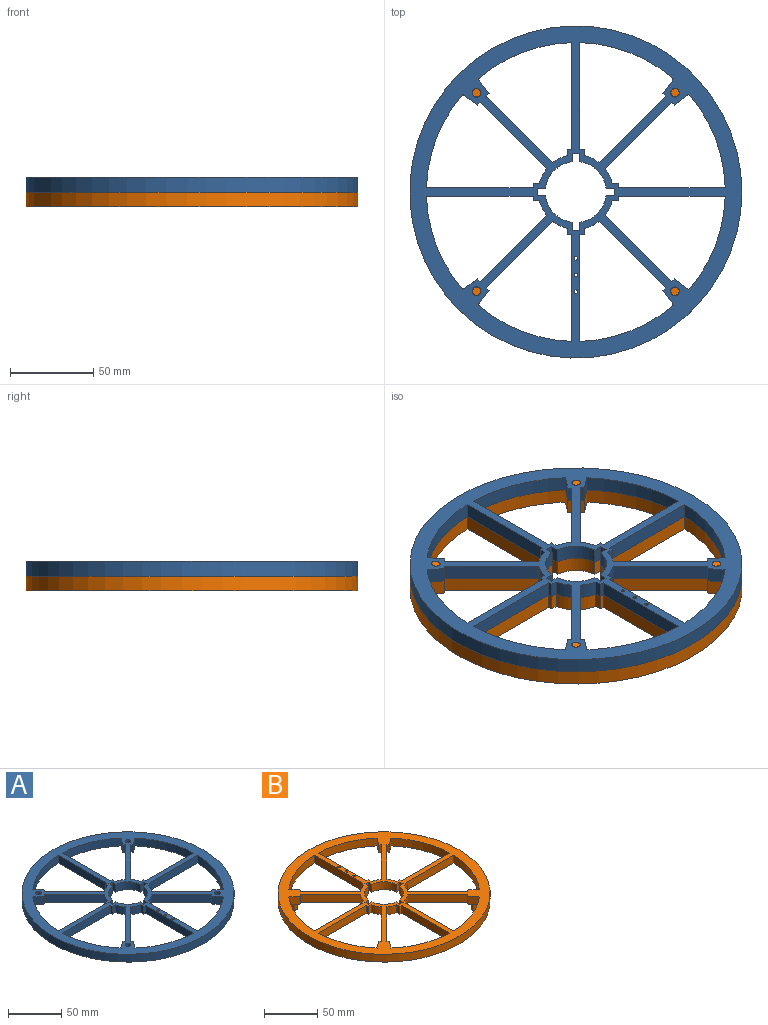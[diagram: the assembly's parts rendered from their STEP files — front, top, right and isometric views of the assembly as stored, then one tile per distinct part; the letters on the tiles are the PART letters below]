
ASSEMBLY  parts=2 mates=1
PART A: 94 faces, bbox 200x200x9 mm
  f0: plane 188.8x188.8mm, normal (0,0,-1), area 5946.6mm2, adj f1,f2,f3,f4,f5,f6,f7,f8
  f1: plane 40.07x40.07mm, normal (-0.71,0.71,0), area 510mm2, adj f0,f2,f75,f89
  f2: plane 9x1.78mm, normal (0.7,0.71,0), area 22.5mm2, adj f0,f1,f3,f89
  f3: plane 9x8.64mm, normal (-0.6,0.8,0), area 97.4mm2, adj f0,f2,f4,f89
  f4: cylinder r=90mm len=56.38mm, axis (0,0,-1), area 555.1mm2, adj f0,f3,f5,f89
  f5: plane 64.26x9mm, normal (0,-1,0), area 578.3mm2, adj f0,f4,f6,f89
  f6: plane 9x2.5mm, normal (-1,0,0), area 22.5mm2, adj f0,f5,f7,f89
  f7: plane 9x3.77mm, normal (0,-1,0), area 33.9mm2, adj f0,f6,f75,f89
  f8: plane 40.07x40.07mm, normal (0.71,0.71,0), area 510mm2, adj f0,f9,f76,f89
  f9: plane 9x1.78mm, normal (0.71,-0.7,0), area 22.5mm2, adj f0,f8,f10,f89
  f10: plane 9x8.64mm, normal (0.8,0.6,0), area 97.4mm2, adj f0,f9,f11,f89
  f11: cylinder r=90mm len=56.38mm, axis (0,0,-1), area 555.1mm2, adj f0,f10,f12,f89
  f12: plane 64.26x9mm, normal (-1,0,0), area 578.3mm2, adj f0,f11,f13,f89
  f13: plane 9x2.5mm, normal (0,1,0), area 22.5mm2, adj f0,f12,f14,f89
  f14: plane 9x3.77mm, normal (-1,0,0), area 33.9mm2, adj f0,f13,f76,f89
  f15: plane 9x5.02mm, normal (0,1,0), area 45.2mm2, adj f0,f16,f79,f89
  f16: cylinder r=18.4mm len=16.07mm, axis (0,0,-1), area 220.4mm2, adj f0,f15,f17,f89
  f17: plane 9x5.02mm, normal (-1,0,0), area 45.2mm2, adj f0,f16,f18,f89
  f18: plane 9x4.4mm, normal (0,1,0), area 39.6mm2, adj f0,f17,f19,f89
  f19: plane 9x5.02mm, normal (1,0,0), area 45.2mm2, adj f0,f18,f20,f89
  f20: cylinder r=18.4mm len=16.07mm, axis (0,0,-1), area 220.4mm2, adj f0,f19,f21,f89
  f21: plane 9x5.02mm, normal (0,1,0), area 45.2mm2, adj f0,f20,f22,f89
  f22: plane 9x4.4mm, normal (1,0,0), area 39.6mm2, adj f0,f21,f23,f89
  f23: plane 9x5.02mm, normal (0,-1,0), area 45.2mm2, adj f0,f22,f24,f89
  f24: cylinder r=18.4mm len=16.07mm, axis (0,0,-1), area 220.4mm2, adj f0,f23,f25,f89
  f25: plane 9x5.02mm, normal (1,0,0), area 45.2mm2, adj f0,f24,f26,f89
  f26: plane 9x4.4mm, normal (0,-1,0), area 39.6mm2, adj f0,f25,f27,f89
  f27: plane 9x5.02mm, normal (-1,0,0), area 45.2mm2, adj f0,f26,f28,f89
  f28: cylinder r=18.4mm len=16.07mm, axis (0,0,-1), area 220.4mm2, adj f0,f27,f29,f89
  f29: plane 9x5.02mm, normal (0,-1,0), area 45.2mm2, adj f0,f28,f79,f89
  f30: cylinder r=90mm len=56.38mm, axis (0,0,-1), area 555.1mm2, adj f0,f31,f80,f89
  f31: plane 9x8.71mm, normal (-0.6,-0.8,0), area 98.2mm2, adj f0,f30,f32,f89
  f32: plane 9x1.78mm, normal (0.71,-0.7,0), area 22.5mm2, adj f0,f31,f33,f89
  f33: plane 40.03x40.03mm, normal (-0.71,-0.71,0), area 509.5mm2, adj f0,f32,f34,f89
  f34: cylinder r=22.5mm len=9.04mm, axis (0,0,-1), area 91.1mm2, adj f0,f33,f35,f89
  f35: plane 9x3.77mm, normal (0,1,0), area 33.9mm2, adj f0,f34,f36,f89
  f36: plane 9x2.5mm, normal (-1,0,0), area 22.5mm2, adj f0,f35,f80,f89
  f37: cylinder r=90mm len=56.38mm, axis (0,0,-1), area 555.1mm2, adj f0,f38,f82,f89
  f38: plane 64.26x9mm, normal (0,1,0), area 578.3mm2, adj f0,f37,f39,f89
  f39: plane 9x2.5mm, normal (1,0,0), area 22.5mm2, adj f0,f38,f40,f89
  f40: plane 9x3.77mm, normal (0,1,0), area 33.9mm2, adj f0,f39,f41,f89
  f41: cylinder r=22.5mm len=9.04mm, axis (0,0,-1), area 91.1mm2, adj f0,f40,f42,f89
  f42: plane 40.07x40.07mm, normal (0.71,-0.71,0), area 510mm2, adj f0,f41,f43,f89
  f43: plane 9x1.78mm, normal (-0.7,-0.71,0), area 22.5mm2, adj f0,f42,f82,f89
  f44: plane 64.26x9mm, normal (0,-1,0), area 578.3mm2, adj f0,f45,f83,f89
  f45: cylinder r=90mm len=56.38mm, axis (0,0,-1), area 555.1mm2, adj f0,f44,f46,f89
  f46: plane 9x8.71mm, normal (0.6,0.8,0), area 98.2mm2, adj f0,f45,f47,f89
  f47: plane 9x1.78mm, normal (-0.71,0.7,0), area 22.5mm2, adj f0,f46,f48,f89
  f48: plane 40.03x40.03mm, normal (0.71,0.71,0), area 509.5mm2, adj f0,f47,f49,f89
  f49: cylinder r=22.5mm len=9.04mm, axis (0,0,-1), area 91.1mm2, adj f0,f48,f50,f89
  f50: plane 9x3.77mm, normal (0,-1,0), area 33.9mm2, adj f0,f49,f83,f89
  f51: cylinder r=90mm len=56.38mm, axis (0,0,-1), area 555.1mm2, adj f0,f52,f85,f89
  f52: plane 9x8.71mm, normal (-0.8,0.6,0), area 98.2mm2, adj f0,f51,f53,f89
  f53: plane 9x1.78mm, normal (-0.7,-0.71,0), area 22.5mm2, adj f0,f52,f54,f89
  f54: plane 40.03x40.03mm, normal (-0.71,0.71,0), area 509.5mm2, adj f0,f53,f55,f89
  f55: cylinder r=22.5mm len=9.04mm, axis (0,0,-1), area 91.1mm2, adj f0,f54,f56,f89
  f56: plane 9x3.77mm, normal (1,0,0), area 33.9mm2, adj f0,f55,f57,f89
  f57: plane 9x2.5mm, normal (0,1,0), area 22.5mm2, adj f0,f56,f85,f89
  f58: plane 64.26x9mm, normal (-1,0,0), area 578.3mm2, adj f0,f59,f86,f89
  f59: cylinder r=90mm len=56.38mm, axis (0,0,-1), area 555.1mm2, adj f0,f58,f60,f89
  f60: plane 9x8.71mm, normal (0.8,-0.6,0), area 98.2mm2, adj f0,f59,f61,f89
  f61: plane 9x1.78mm, normal (0.7,0.71,0), area 22.5mm2, adj f0,f60,f62,f89
  f62: plane 40.03x40.03mm, normal (0.71,-0.71,0), area 509.5mm2, adj f0,f61,f63,f89
  f63: cylinder r=22.5mm len=9.04mm, axis (0,0,-1), area 91.1mm2, adj f0,f62,f64,f89
  f64: plane 9x3.77mm, normal (-1,0,0), area 33.9mm2, adj f0,f63,f86,f89
  f65: cylinder r=90mm len=56.38mm, axis (0,0,-1), area 555.1mm2, adj f0,f66,f87,f89
  f66: plane 64.26x9mm, normal (1,0,0), area 578.3mm2, adj f0,f65,f67,f89
  f67: plane 9x2.5mm, normal (0,-1,0), area 22.5mm2, adj f0,f66,f68,f89
  f68: plane 9x3.77mm, normal (1,0,0), area 33.9mm2, adj f0,f67,f69,f89
  f69: cylinder r=22.5mm len=9.04mm, axis (0,0,-1), area 91.1mm2, adj f0,f68,f70,f89
  f70: plane 40.07x40.07mm, normal (-0.71,-0.71,0), area 510mm2, adj f0,f69,f71,f89
  f71: plane 9x1.78mm, normal (-0.71,0.7,0), area 22.5mm2, adj f0,f70,f87,f89
  f72: cylinder r=1.1mm len=9mm, axis (0,0,-1), area 62.2mm2, adj f0,f89
  f73: cylinder r=1.1mm len=9mm, axis (0,0,-1), area 62.2mm2, adj f0,f89
  f74: cylinder r=2.62mm len=9mm, axis (0,0,-1), area 148.4mm2, adj f0,f89
  f75: cylinder r=22.5mm len=9.04mm, axis (0,0,-1), area 91.1mm2, adj f0,f1,f7,f89
  f76: cylinder r=22.5mm len=9.04mm, axis (0,0,-1), area 91.1mm2, adj f0,f8,f14,f89
  f77: cylinder r=100mm len=200mm, axis (0,0,-1), area 5654.9mm2, adj f89,f90
  f78: cylinder r=2.62mm len=9mm, axis (0,0,-1), area 148.4mm2, adj f0,f89
  f79: plane 9x4.4mm, normal (-1,0,0), area 39.6mm2, adj f0,f15,f29,f89
  f80: plane 64.26x9mm, normal (0,1,0), area 578.3mm2, adj f0,f30,f36,f89
  f81: cylinder r=2.62mm len=9mm, axis (0,0,-1), area 148.4mm2, adj f0,f89
  f82: plane 9x8.64mm, normal (0.6,-0.8,0), area 97.4mm2, adj f0,f37,f43,f89
  f83: plane 9x2.5mm, normal (1,0,0), area 22.5mm2, adj f0,f44,f50,f89
  f84: cylinder r=2.62mm len=9mm, axis (0,0,-1), area 148.4mm2, adj f0,f89
  f85: plane 64.26x9mm, normal (1,0,0), area 578.3mm2, adj f0,f51,f57,f89
  f86: plane 9x2.5mm, normal (0,-1,0), area 22.5mm2, adj f0,f58,f64,f89
  f87: plane 9x8.64mm, normal (-0.8,-0.6,0), area 97.4mm2, adj f0,f65,f71,f89
  f88: cylinder r=1.1mm len=9mm, axis (0,0,-1), area 62.2mm2, adj f0,f89
  f89: plane 200x200mm, normal (0,0,1), area 9366.7mm2, adj f1,f2,f3,f4,f5,f6,f7,f8
  f90: plane 200x200mm, normal (0,0,-1), area 2703.8mm2, adj f77,f91
  f91: cylinder r=95.6mm len=191.2mm, axis (0,0,-1), area 901mm2, adj f90,f93
  f92: cylinder r=94.4mm len=188.8mm, axis (0,0,-1), area 889.7mm2, adj f0,f93
  f93: plane 191.2x191.2mm, normal (0,0,-1), area 716.3mm2, adj f91,f92
PART B: 98 faces, bbox 200x200x18 mm
  f0: plane 188.8x188.8mm, normal (0,0,-1), area 5954.7mm2, adj f1,f2,f3,f4,f5,f6,f7,f8
  f1: plane 40.03x40.03mm, normal (-0.71,0.71,0), area 509.5mm2, adj f0,f2,f73,f84
  f2: cylinder r=22.5mm len=9.04mm, axis (0,0,-1), area 91.1mm2, adj f0,f1,f3,f84
  f3: plane 9x3.77mm, normal (1,0,0), area 33.9mm2, adj f0,f2,f4,f84
  f4: plane 9x2.5mm, normal (0,1,0), area 22.5mm2, adj f0,f3,f5,f84
  f5: plane 64.26x9mm, normal (1,0,0), area 578.3mm2, adj f0,f4,f6,f84
  f6: cylinder r=90mm len=56.38mm, axis (0,0,-1), area 555.1mm2, adj f0,f5,f7,f84
  f7: plane 9x8.71mm, normal (-0.8,0.6,0), area 98.2mm2, adj f0,f6,f73,f84
  f8: plane 9x8.64mm, normal (0.6,-0.8,0), area 97.4mm2, adj f0,f9,f74,f84
  f9: cylinder r=90mm len=56.38mm, axis (0,0,-1), area 555.1mm2, adj f0,f8,f10,f84
  f10: plane 64.26x9mm, normal (0,1,0), area 578.3mm2, adj f0,f9,f11,f84
  f11: plane 9x2.5mm, normal (1,0,0), area 22.5mm2, adj f0,f10,f12,f84
  f12: plane 9x3.77mm, normal (0,1,0), area 33.9mm2, adj f0,f11,f13,f84
  f13: cylinder r=22.5mm len=9.04mm, axis (0,0,-1), area 91.1mm2, adj f0,f12,f14,f84
  f14: plane 40.07x40.07mm, normal (0.71,-0.71,0), area 510mm2, adj f0,f13,f74,f84
  f15: cylinder r=90mm len=56.38mm, axis (0,0,-1), area 555.1mm2, adj f0,f16,f75,f84
  f16: plane 9x8.71mm, normal (0.6,0.8,0), area 98.2mm2, adj f0,f15,f17,f84
  f17: plane 9x1.78mm, normal (-0.71,0.7,0), area 22.5mm2, adj f0,f16,f18,f84
  f18: plane 40.03x40.03mm, normal (0.71,0.71,0), area 509.5mm2, adj f0,f17,f19,f84
  f19: cylinder r=22.5mm len=9.04mm, axis (0,0,-1), area 91.1mm2, adj f0,f18,f20,f84
  f20: plane 9x3.77mm, normal (0,-1,0), area 33.9mm2, adj f0,f19,f21,f84
  f21: plane 9x2.5mm, normal (1,0,0), area 22.5mm2, adj f0,f20,f75,f84
  f22: cylinder r=22.5mm len=9.04mm, axis (0,0,-1), area 91.1mm2, adj f0,f23,f76,f84
  f23: plane 40.07x40.07mm, normal (-0.71,-0.71,0), area 510mm2, adj f0,f22,f24,f84
  f24: plane 9x1.78mm, normal (-0.71,0.7,0), area 22.5mm2, adj f0,f23,f25,f84
  f25: plane 9x8.64mm, normal (-0.8,-0.6,0), area 97.4mm2, adj f0,f24,f26,f84
  f26: cylinder r=90mm len=56.38mm, axis (0,0,-1), area 555.1mm2, adj f0,f25,f27,f84
  f27: plane 64.26x9mm, normal (1,0,0), area 578.3mm2, adj f0,f26,f28,f84
  f28: plane 9x2.5mm, normal (0,-1,0), area 22.5mm2, adj f0,f27,f76,f84
  f29: plane 9x5.02mm, normal (0,1,0), area 45.2mm2, adj f0,f30,f77,f84
  f30: cylinder r=18.4mm len=16.07mm, axis (0,0,-1), area 220.4mm2, adj f0,f29,f31,f84
  f31: plane 9x5.02mm, normal (-1,0,0), area 45.2mm2, adj f0,f30,f32,f84
  f32: plane 9x4.4mm, normal (0,1,0), area 39.6mm2, adj f0,f31,f33,f84
  f33: plane 9x5.02mm, normal (1,0,0), area 45.2mm2, adj f0,f32,f34,f84
  f34: cylinder r=18.4mm len=16.07mm, axis (0,0,-1), area 220.4mm2, adj f0,f33,f35,f84
  f35: plane 9x5.02mm, normal (0,1,0), area 45.2mm2, adj f0,f34,f36,f84
  f36: plane 9x4.4mm, normal (1,0,0), area 39.6mm2, adj f0,f35,f37,f84
  f37: plane 9x5.02mm, normal (0,-1,0), area 45.2mm2, adj f0,f36,f38,f84
  f38: cylinder r=18.4mm len=16.07mm, axis (0,0,-1), area 220.4mm2, adj f0,f37,f39,f84
  f39: plane 9x5.02mm, normal (1,0,0), area 45.2mm2, adj f0,f38,f40,f84
  f40: plane 9x4.4mm, normal (0,-1,0), area 39.6mm2, adj f0,f39,f41,f84
  f41: plane 9x5.02mm, normal (-1,0,0), area 45.2mm2, adj f0,f40,f42,f84
  f42: cylinder r=18.4mm len=16.07mm, axis (0,0,-1), area 220.4mm2, adj f0,f41,f43,f84
  f43: plane 9x5.02mm, normal (0,-1,0), area 45.2mm2, adj f0,f42,f77,f84
  f44: plane 9x8.64mm, normal (0.8,0.6,0), area 97.4mm2, adj f0,f45,f78,f84
  f45: cylinder r=90mm len=56.38mm, axis (0,0,-1), area 555.1mm2, adj f0,f44,f46,f84
  f46: plane 64.26x9mm, normal (-1,0,0), area 578.3mm2, adj f0,f45,f47,f84
  f47: plane 9x2.5mm, normal (0,1,0), area 22.5mm2, adj f0,f46,f48,f84
  f48: plane 9x3.77mm, normal (-1,0,0), area 33.9mm2, adj f0,f47,f49,f84
  f49: cylinder r=22.5mm len=9.04mm, axis (0,0,-1), area 91.1mm2, adj f0,f48,f50,f84
  f50: plane 40.07x40.07mm, normal (0.71,0.71,0), area 510mm2, adj f0,f49,f78,f84
  f51: plane 9x1.78mm, normal (0.7,0.71,0), area 22.5mm2, adj f0,f52,f79,f84
  f52: plane 40.03x40.03mm, normal (0.71,-0.71,0), area 509.5mm2, adj f0,f51,f53,f84
  f53: cylinder r=22.5mm len=9.04mm, axis (0,0,-1), area 91.1mm2, adj f0,f52,f54,f84
  f54: plane 9x3.77mm, normal (-1,0,0), area 33.9mm2, adj f0,f53,f55,f84
  f55: plane 9x2.5mm, normal (0,-1,0), area 22.5mm2, adj f0,f54,f56,f84
  f56: plane 64.26x9mm, normal (-1,0,0), area 578.3mm2, adj f0,f55,f57,f84
  f57: cylinder r=90mm len=56.38mm, axis (0,0,-1), area 555.1mm2, adj f0,f56,f79,f84
  f58: plane 40.07x40.07mm, normal (-0.71,0.71,0), area 510mm2, adj f0,f59,f80,f84
  f59: plane 9x1.78mm, normal (0.7,0.71,0), area 22.5mm2, adj f0,f58,f60,f84
  f60: plane 9x8.64mm, normal (-0.6,0.8,0), area 97.4mm2, adj f0,f59,f61,f84
  f61: cylinder r=90mm len=56.38mm, axis (0,0,-1), area 555.1mm2, adj f0,f60,f62,f84
  f62: plane 64.26x9mm, normal (0,-1,0), area 578.3mm2, adj f0,f61,f63,f84
  f63: plane 9x2.5mm, normal (-1,0,0), area 22.5mm2, adj f0,f62,f64,f84
  f64: plane 9x3.77mm, normal (0,-1,0), area 33.9mm2, adj f0,f63,f80,f84
  f65: cylinder r=90mm len=56.38mm, axis (0,0,-1), area 555.1mm2, adj f0,f66,f81,f84
  f66: plane 9x8.71mm, normal (-0.6,-0.8,0), area 98.2mm2, adj f0,f65,f67,f84
  f67: plane 9x1.78mm, normal (0.71,-0.7,0), area 22.5mm2, adj f0,f66,f68,f84
  f68: plane 40.03x40.03mm, normal (-0.71,-0.71,0), area 509.5mm2, adj f0,f67,f69,f84
  f69: cylinder r=22.5mm len=9.04mm, axis (0,0,-1), area 91.1mm2, adj f0,f68,f70,f84
  f70: plane 9x3.77mm, normal (0,1,0), area 33.9mm2, adj f0,f69,f71,f84
  f71: plane 9x2.5mm, normal (-1,0,0), area 22.5mm2, adj f0,f70,f81,f84
  f72: cylinder r=1.1mm len=9mm, axis (0,0,-1), area 62.2mm2, adj f0,f84
  f73: plane 9x1.78mm, normal (-0.7,-0.71,0), area 22.5mm2, adj f0,f1,f7,f84
  f74: plane 9x1.78mm, normal (-0.7,-0.71,0), area 22.5mm2, adj f0,f8,f14,f84
  f75: plane 64.26x9mm, normal (0,-1,0), area 578.3mm2, adj f0,f15,f21,f84
  f76: plane 9x3.77mm, normal (1,0,0), area 33.9mm2, adj f0,f22,f28,f84
  f77: plane 9x4.4mm, normal (-1,0,0), area 39.6mm2, adj f0,f29,f43,f84
  f78: plane 9x1.78mm, normal (0.71,-0.7,0), area 22.5mm2, adj f0,f44,f50,f84
  f79: plane 9x8.71mm, normal (0.8,-0.6,0), area 98.2mm2, adj f0,f51,f57,f84
  f80: cylinder r=22.5mm len=9.04mm, axis (0,0,-1), area 91.1mm2, adj f0,f58,f64,f84
  f81: plane 64.26x9mm, normal (0,1,0), area 578.3mm2, adj f0,f65,f71,f84
  f82: cylinder r=100mm len=200mm, axis (0,0,-1), area 5654.9mm2, adj f84,f85
  f83: cylinder r=1.1mm len=9mm, axis (0,0,-1), area 62.2mm2, adj f0,f84
  f84: plane 200x200mm, normal (0,0,1), area 9453.3mm2, adj f1,f2,f3,f4,f5,f6,f7,f8
  f85: plane 200x200mm, normal (0,0,-1), area 2703.8mm2, adj f82,f86
  f86: cylinder r=95.6mm len=191.2mm, axis (0,0,-1), area 901mm2, adj f85,f88
  f87: cylinder r=94.4mm len=188.8mm, axis (0,0,-1), area 889.7mm2, adj f0,f88
  f88: plane 191.2x191.2mm, normal (0,0,-1), area 716.3mm2, adj f86,f87
  f89: cylinder r=1.1mm len=9mm, axis (0,0,-1), area 62.2mm2, adj f0,f84
  f90: cylinder r=2.5mm len=9mm, axis (0,0,-1), area 141.4mm2, adj f0,f91
  f91: plane 5x5mm, normal (0,0,-1), area 19.6mm2, adj f90
  f92: cylinder r=2.5mm len=9mm, axis (0,0,-1), area 141.4mm2, adj f0,f93
  f93: plane 5x5mm, normal (0,0,-1), area 19.6mm2, adj f92
  f94: cylinder r=2.5mm len=9mm, axis (0,0,-1), area 141.4mm2, adj f0,f95
  f95: plane 5x5mm, normal (0,0,-1), area 19.6mm2, adj f94
  f96: cylinder r=2.5mm len=9mm, axis (0,0,-1), area 141.4mm2, adj f0,f97
  f97: plane 5x5mm, normal (0,0,-1), area 19.6mm2, adj f96
PLACE A t=(328.32,82.87,-21.04)mm
PLACE B rot(axis=(1,0,0),180deg) t=(94.62,43.6,-21.04)mm
MATE fastened B.f2 <-> A.f4  axis (0,0,1) through (94.62,43.6,-21.04)mm
